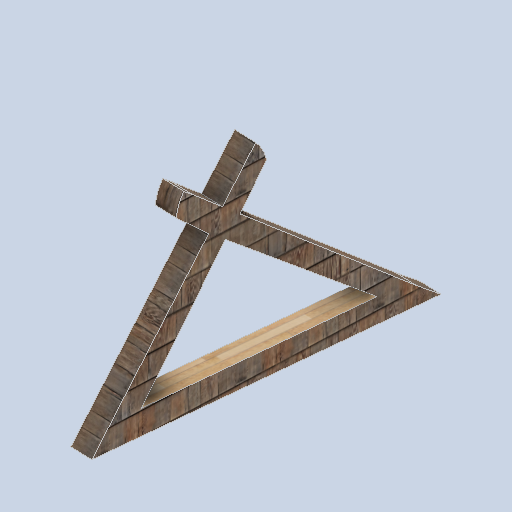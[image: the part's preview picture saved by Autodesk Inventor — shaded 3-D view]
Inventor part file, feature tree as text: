
AUTODESK INVENTOR PART (.ipt)
format: ipt  version: 2024.2 (Build 282272000, 272)  size: 216,576 bytes
history: native  units: in
note: dims shown in document units (in); Inventor stores cm internally (conversion verified against a paired STEP export)
features: sketch x9, plane x6, other x3
ambient origin geometry x8: Origin, YZ Plane, XZ Plane, XY Plane, X Axis, Y Axis, Z Axis, Center Point
bodies: Solid1 (feature_tree)
feature tree (18):
  other  "pad_outframe_03.ipt"
  other  "Solid1::pad_outframe_03.ipt"
  other  "TaggingFeature1"
  sketch  "Sketch1"  dims[d0=0.3937in]
  sketch  "Sketch2"
  sketch  "Sketch3"
  sketch  "Sketch6"
  sketch  "Sketch7"
  sketch  "Sketch8"
  sketch  "Sketch9"
  sketch  "Sketch10"
  sketch  "Sketch11"
  plane  "Work Plane1"
  plane  "Work Plane2"
  plane  "Work Plane3"
  plane  "Work Plane4"
  plane  "Work Plane5"
  plane  "Work Plane6"
